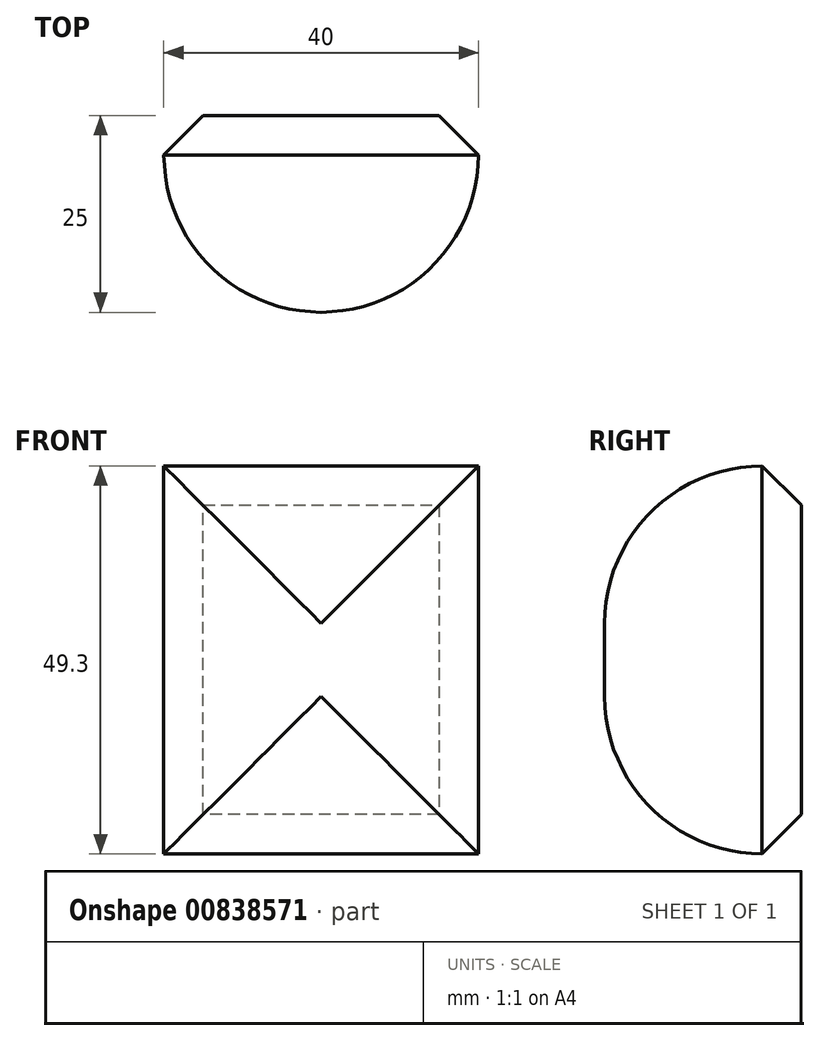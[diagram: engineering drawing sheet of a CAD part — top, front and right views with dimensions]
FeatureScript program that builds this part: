
annotation { "Feature Type Name" : "Feature", "Feature Type Description" : "" }
export const myFeature = defineFeature(function(context is Context, id is Id, definition is map)
    precondition{}
    {
        {
            var Q0;
            Q0=qCreatedBy(makeId("Top.planeOp"),FACE);
            var sketch = newSketch(context, id + "F0", { "sketchPlane" : qUnion([Q0])});
            skLineSegment(sketch, "E0.bottom", {"start": v(-44.3, -26.4) * mm, "end": v(-4.3, -26.4) * mm});
            skLineSegment(sketch, "E0.top", {"start": v(-44.3, -1.4) * mm, "end": v(-4.3, -1.4) * mm});
            skLineSegment(sketch, "E0.left", {"start": v(-44.3, -26.4) * mm, "end": v(-44.3, -1.4) * mm});
            skLineSegment(sketch, "E0.right", {"start": v(-4.3, -26.4) * mm, "end": v(-4.3, -1.4) * mm});
            skSolve(sketch);
        }
        {
            var Q0;
            Q0=makeQuery(id+"F0.imprint","IMPRINT",FACE,{"disambiguationData":[TD([[makeQuery(id+"F0.imprint","IMPRINT",EDGE,{"derivedFrom":sQuery(id+"F0.wireOp",EDGE,"E0.bottom")}),1.0]])]});
            extrude(context, id + "F1", {"entities" : qUnion([Q0]), "depth" : 49.3 * mm, "offsetDistance" : 25 * mm});
        }
        {
            var Q0;
            Q0=makeQuery(id+"F1.opExtrude","SWEPT_FACE",FACE,{"disambiguationData":[OSD([sQuery(id+"F0.wireOp",EDGE,"E0.bottom")])]});
            fillet(context, id + "F2", {"entities" : qUnion([Q0]), "radius" : 20 * mm, "tangentPropagation" : true, "allowEdgeOverflow" : false});
        }
        {
            var Q0;
            Q0=makeQuery(id+"F1.opExtrude","SWEPT_FACE",FACE,{"disambiguationData":[OSD([sQuery(id+"F0.wireOp",EDGE,"E0.top")])]});
            chamfer(context, id + "F3", {"entities" : qUnion([Q0]), "width" : 5 * mm, "tangentPropagation" : true});
        }
    });
